# Revit family: DOMO SENSIA-L PILA
name_source: partatom
category: Aparatos sanitarios
revit_build: Autodesk Revit 2015 (Build: 20140223_1515(x64)
units: mm (PartAtom-declared; Revit-internal decimal feet)

## types (1)
- 79000
    CAUDAL = 6 L/Min
    Comentarios de tipo = ◦Ahorro de agua y energía
◦Proceso automático de adaptación al medio
◦Componentes integrados: mantenimiento sencillo y excelente estanqueidad
◦Conexiones internas estancas
◦Cierre automático en caso de pila agotada
◦Aclarado automático cada 24h
◦Suministrado con: Elementos de fijación, junta y arandela
◦2 latiguillos flexibles de 350 mm, con tuercas de ½”
◦2 válvulas antirretorno
◦2 llaves de paso en escuadra con entrada de ½” y salida de ½”
◦Batería CPR2 o alimentador 12 V según modelo
◦Transformador
    Conexión AC = Sí
    Conexión AF = Sí
    Código de montaje = C1030220
    Descripción = Grifo electrónico para lavabo mezclador, fijación sobre repisa.
    ENTRADA = Macho 1/2"
    Elevación por defecto = 1219 mm
    Fabricante = PRESTO IBÉRICA
    Imagen de tipo = <Ninguno>
    Material = LATON CROMADO
    Modelo = PRESTO DOMO SENSIA L
    PESO BRUTO = 1.300 Kg
    Presión Máxima = 8 bar
    REFERENCIA = 79000
    Teléfono = (+34) 915 782 575
    URL = http://www.prestoiberica.com

## geometry (parser evidence)
native form markers: Blend x3
no freeform markers — native parametric forms only
